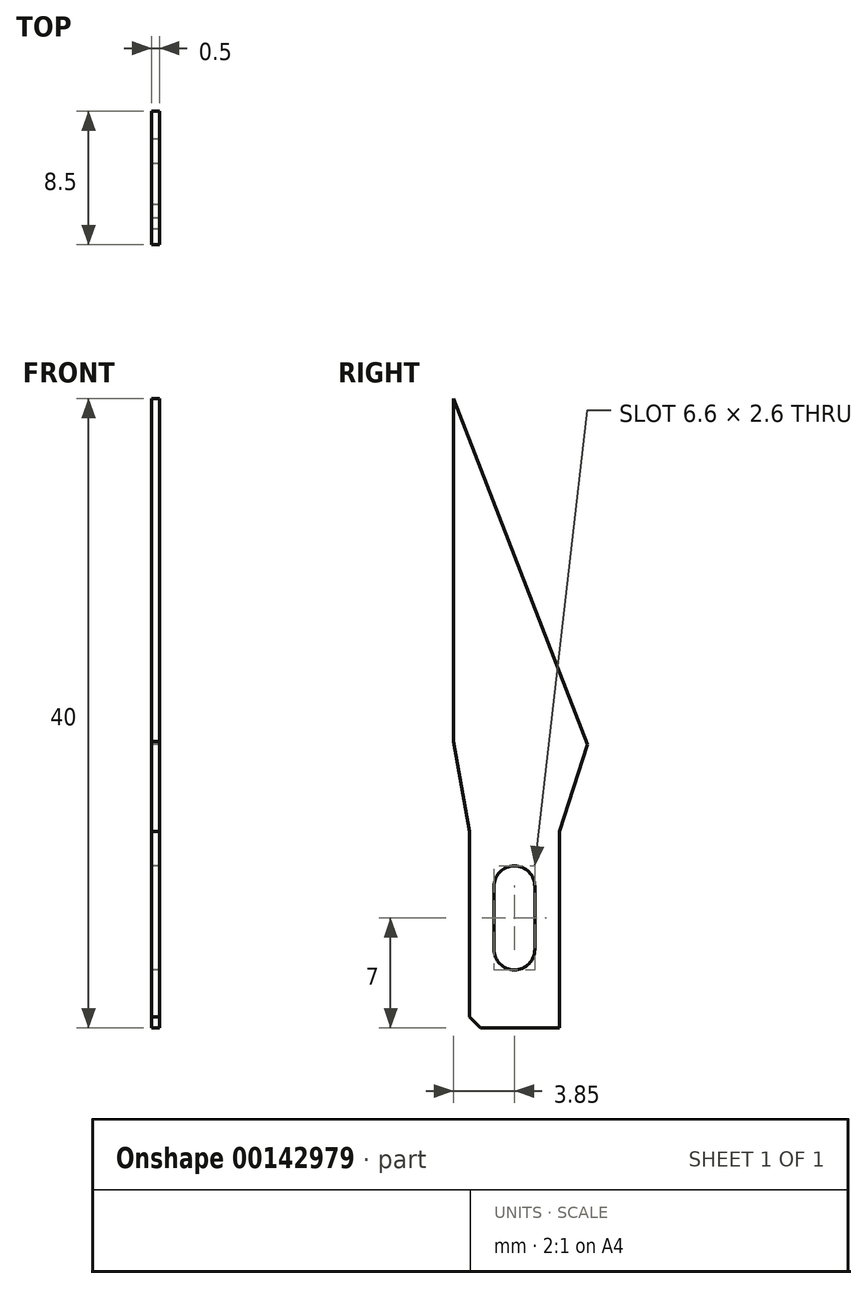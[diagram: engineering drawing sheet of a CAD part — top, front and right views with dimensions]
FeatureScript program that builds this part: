
annotation { "Feature Type Name" : "Feature", "Feature Type Description" : "" }
export const myFeature = defineFeature(function(context is Context, id is Id, definition is map)
    precondition{}
    {
        {
            var Q0;
            Q0=qCreatedBy(makeId("Right.planeOp"),FACE);
            var sketch = newSketch(context, id + "F0", { "sketchPlane" : qUnion([Q0])});
            skLineSegment(sketch, "E0", {"start": v(1.7, -40) * mm, "end": v(6.7, -40) * mm});
            skLineSegment(sketch, "E1", {"start": v(6.7, -40) * mm, "end": v(6.7, -27.5) * mm});
            skLineSegment(sketch, "E2", {"start": v(8.5, -22) * mm, "end": v(0, 0) * mm});
            skLineSegment(sketch, "E3", {"start": v(1, -39.3) * mm, "end": v(1, -27.5) * mm});
            skLineSegment(sketch, "E4", {"start": v(0, -21.8) * mm, "end": v(0, 0) * mm});
            skLineSegment(sketch, "E5", {"start": v(0, -21.8) * mm, "end": v(1, -27.5) * mm});
            skLineSegment(sketch, "E6", {"start": v(6.7, -27.5) * mm, "end": v(8.5, -22) * mm});
            skLineSegment(sketch, "E7", {"start": v(1, -39.3) * mm, "end": v(1.7, -40) * mm});
            skLineSegment(sketch, "E8", {"start": v(1, -27.5) * mm, "end": v(6.7, -27.5) * mm, "construction": true});
            skLineSegment(sketch, "E9.left", {"start": v(2.55, -35) * mm, "end": v(2.55, -31) * mm});
            skLineSegment(sketch, "E9.right", {"start": v(5.15, -35) * mm, "end": v(5.15, -31) * mm});
            skArc(sketch, "E10", {"start": v(2.55, -31) * mm, "mid": v(3.85, -29.7) * mm, "end": v(5.15, -31) * mm});
            skArc(sketch, "E11", {"start": v(5.15, -35) * mm, "mid": v(3.85, -36.3) * mm, "end": v(2.55, -35) * mm});
            skLineSegment(sketch, "E12", {"start": v(2.55, -31) * mm, "end": v(5.15, -31) * mm, "construction": true});
            skSolve(sketch);
        }
        {
            var Q0;
            Q0 = qSketchRegion(id + "F0", true);
            extrude(context, id + "F1", {"entities" : qUnion([Q0]), "endBound" : BoundingType.SYMMETRIC, "depth" : 0.5 * mm});
        }
    });
